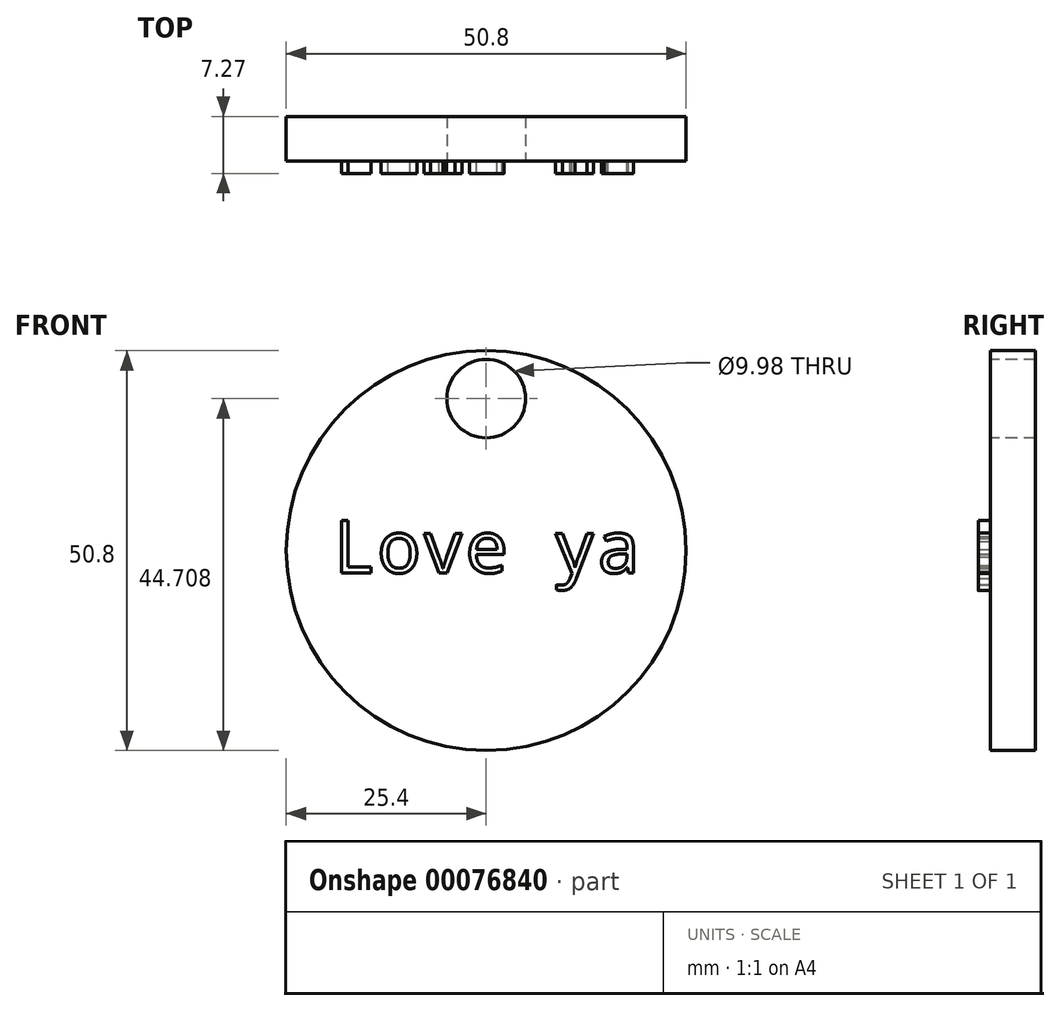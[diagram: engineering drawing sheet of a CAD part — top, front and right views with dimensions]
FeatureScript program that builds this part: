
annotation { "Feature Type Name" : "Feature", "Feature Type Description" : "" }
export const myFeature = defineFeature(function(context is Context, id is Id, definition is map)
    precondition{}
    {
        {
            var Q0;
            Q0=qCreatedBy(makeId("Front.planeOp"),FACE);
            var sketch = newSketch(context, id + "F0", { "sketchPlane" : qUnion([Q0])});
            skCircle(sketch, "E0", {"center": v(0, 0) * mm, "radius": 25.4 * mm});
            skLineSegment(sketch, "E1", {"start": v(0, 25.4) * mm, "end": v(0, 0) * mm, "construction": true});
            skLineSegment(sketch, "E2", {"start": v(0, 0) * mm, "end": v(0, -25.4) * mm, "construction": true});
            skLineSegment(sketch, "E3", {"start": v(-25.4, 0) * mm, "end": v(0, 0) * mm, "construction": true});
            skLineSegment(sketch, "E4", {"start": v(0, 0) * mm, "end": v(25.4, 0) * mm, "construction": true});
            skSolve(sketch);
        }
        {
            var Q0;
            Q0 = qSketchRegion(id + "F0", true);
            extrude(context, id + "F1", {"entities" : qUnion([Q0]), "depth" : 5.7 * mm});
        }
        {
            var Q0;
            Q0=makeQuery(id+"F1.opExtrude","CAP_FACE",FACE,{"disambiguationData":[OSD([sQuery(id+"F0.wireOp",EDGE,"E0")])],"isStart":false});
            var sketch = newSketch(context, id + "F2", { "sketchPlane" : qUnion([Q0])});
            skCircle(sketch, "E5", {"center": v(0, 19.3) * mm, "radius": 4.99 * mm});
            skSolve(sketch);
        }
        {
            var Q0;
            Q0 = qSketchRegion(id + "F2", true);
            extrude(context, id + "F3", {"entities" : qUnion([Q0]), "operationType" : NewBodyOperationType.REMOVE, "oppositeDirection" : true, "depth" : 25.4 * mm});
        }
        {
            var Q0;
            Q0=makeQuery(id+"F1.opExtrude","CAP_FACE",FACE,{"disambiguationData":[OSD([sQuery(id+"F0.wireOp",EDGE,"E0")])],"isStart":false});
            var sketch = newSketch(context, id + "F4", { "sketchPlane" : qUnion([Q0])});
            skText(sketch, "E6", { "text": "Love ya ", "fontName": "DroidSansMono.ttf"});
            const initialGuessF4  = {"E6": [-0.01944, -0.00283, 1, 0, 0.00669]};
            skSetInitialGuess(sketch, initialGuessF4);
            skSolve(sketch);
        }
        {
            var Q0;
            Q0 = qSketchRegion(id + "F4", true);
            extrude(context, id + "F5", {"entities" : qUnion([Q0]), "operationType" : NewBodyOperationType.ADD, "depth" : 1.56 * mm});
        }
    });
